# Revit family: External block S730_S900_3R1A
name_source: partatom
category: Оборудование
units: mm (PartAtom-declared; Revit-internal decimal feet)

## family parameters
Всегда вертикально = Да
Классификация = Нет
На основе рабочей плоскости = Нет
Общий = Нет
При загрузке вырезать с полостями = Нет
Размер круглого соединителя = Использовать диаметр
Тип детали = Нормальный
Точка принадлежности помещению = Нет

## types (4) — shared parameters
00_20_Manufacturer = BLAUBERG
00_20_Name = External block
A = 2020 мм
B = 400 мм
C = 1740 мм
Casing Material = Steel, white, mat
Cp = 790 мм
Cv = 445 мм
D = 586 мм
Dv = 740 мм
E = 840 мм
Grid Material = Mesh, steel, painted,  white
Height = 1740 мм
Lb = 1990 мм
Length = 2020 мм
Load Classification = HVAC
Lv = 575 мм
Maintenance zone material = <По категории>
Maximum Air Flow = 0.0 л/с
Pressure_Static_Air = 0.0 Па
Width = 400 мм
d = 16 мм
d1 = 35 мм
h = 1720 мм
rn = 10 мм
wn = 268 мм
Изготовитель = BLAUBERG
zero-valued in all types: Отметка по умолчанию

## per-type parameters (varying)
| type | Power | Weight |
| BLHVE-S730-O/3R1A | 16780 Вт | 433.00 кг |
| BLHVE-S785-O/3R1A | 18500 Вт | 433.00 кг |
| BLHVE-S850-O/3R1A | 21350 Вт | 480.00 кг |
| BLHVE-S900-O/3R1A | 24330 Вт | 480.00 кг |

note: column(s) folded — value = type name in every type: 00_20_Type
